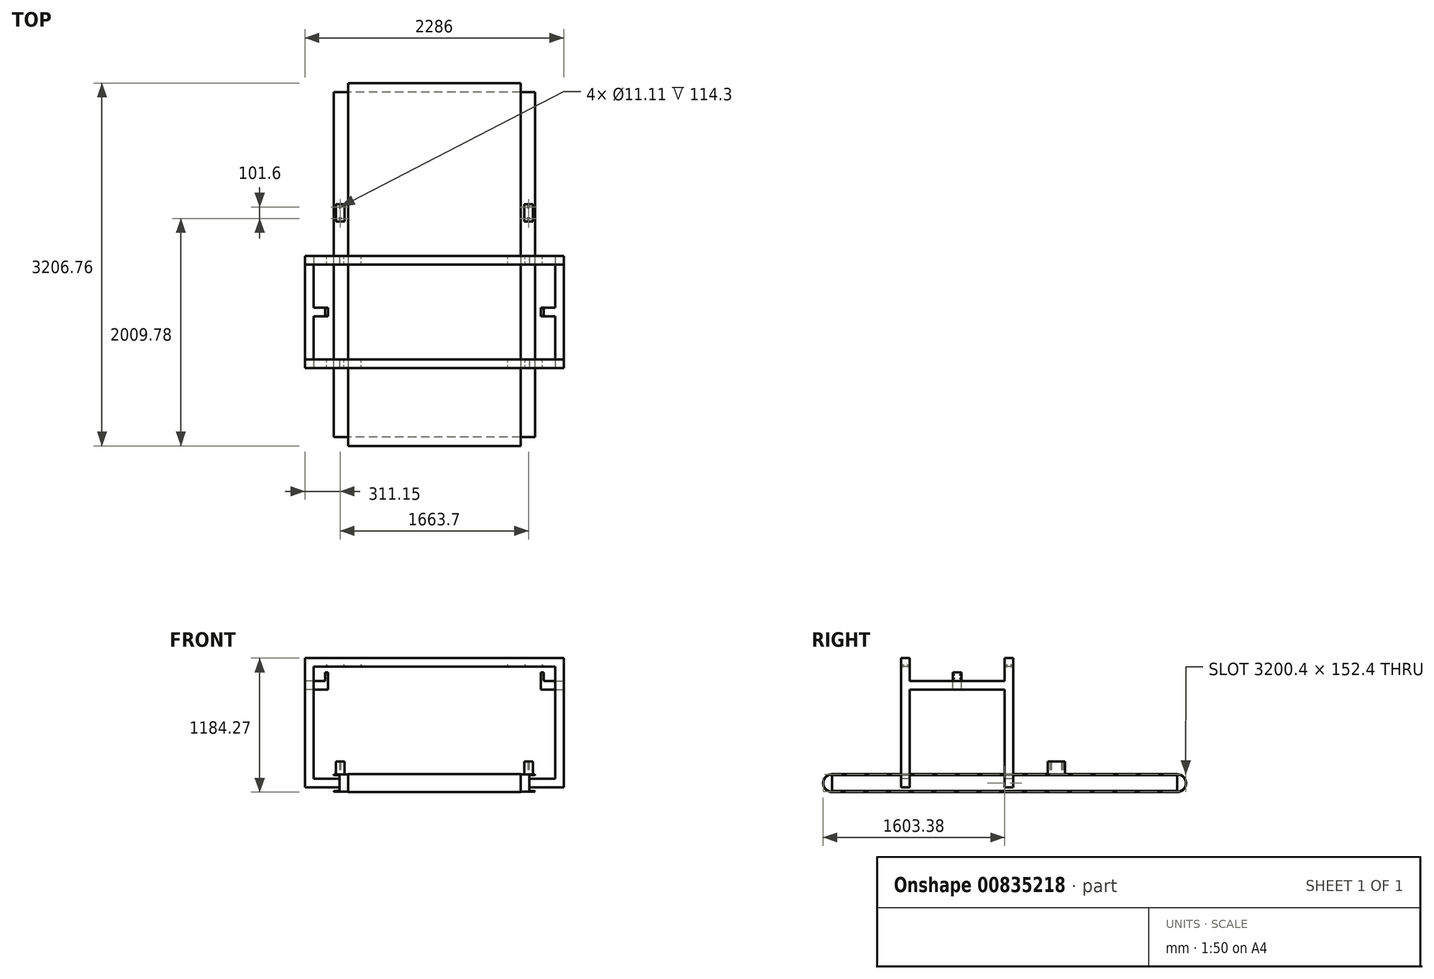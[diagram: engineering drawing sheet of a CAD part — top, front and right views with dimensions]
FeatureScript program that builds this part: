
annotation { "Feature Type Name" : "Feature", "Feature Type Description" : "" }
export const myFeature = defineFeature(function(context is Context, id is Id, definition is map)
    precondition{}
    {
        {
            var Q0;
            Q0=qCreatedBy(makeId("Right.planeOp"),FACE);
            var sketch = newSketch(context, id + "F0", { "sketchPlane" : qUnion([Q0])});
            skLineSegment(sketch, "E0.bottom", {"start": v(1524, 1.59) * mm, "end": v(-1524, 1.59) * mm});
            skLineSegment(sketch, "E0.top", {"start": v(1524, -1.59) * mm, "end": v(-1524, -1.59) * mm});
            skLineSegment(sketch, "E0.left", {"start": v(1524, 1.59) * mm, "end": v(1524, -1.59) * mm});
            skPoint(sketch, "E0.middle", {"position": v(0, 0) * mm});
            skArc(sketch, "E1", {"start": v(-1524, -1.59) * mm, "mid": v(-1600.2, -77.79) * mm, "end": v(-1524, -153.99) * mm});
            skLineSegment(sketch, "E2.0", {"start": v(1524, -153.99) * mm, "end": v(-1524, -153.99) * mm});
            skLineSegment(sketch, "E3.0", {"start": v(1524, -157.16) * mm, "end": v(-1524, -157.16) * mm});
            skArc(sketch, "E4", {"start": v(-1524, 1.59) * mm, "mid": v(-1603.38, -77.79) * mm, "end": v(-1524, -157.16) * mm});
            skArc(sketch, "E5", {"start": v(1524, -153.99) * mm, "mid": v(1600.2, -77.79) * mm, "end": v(1524, -1.59) * mm});
            skArc(sketch, "E6", {"start": v(1524, -157.16) * mm, "mid": v(1603.38, -77.79) * mm, "end": v(1524, 1.59) * mm});
            skSolve(sketch);
        }
        {
            var Q0;
            Q0 = qSketchRegion(id + "F0", true);
            extrude(context, id + "F1", {"entities" : qUnion([Q0]), "endBound" : BoundingType.SYMMETRIC, "depth" : 1524 * mm, "offsetDistance" : 25.4 * mm});
        }
        {
            var Q0;
            Q0=qCreatedBy(makeId("Front.planeOp"),FACE);
            var sketch = newSketch(context, id + "F2", { "sketchPlane" : qUnion([Q0])});
            skLineSegment(sketch, "E7", {"start": v(889, -153.99) * mm, "end": v(-889, -153.99) * mm});
            skLineSegment(sketch, "E8", {"start": v(-889, -153.99) * mm, "end": v(-889, -147.64) * mm});
            skLineSegment(sketch, "E9", {"start": v(-889, -147.64) * mm, "end": v(-838.2, -147.64) * mm});
            skLineSegment(sketch, "E10", {"start": v(-838.2, -147.64) * mm, "end": v(-838.2, -7.94) * mm});
            skLineSegment(sketch, "E11", {"start": v(-838.2, -7.94) * mm, "end": v(-889, -7.94) * mm});
            skLineSegment(sketch, "E12", {"start": v(0, 86.65) * mm, "end": v(0, -258.01) * mm, "construction": true});
            skLineSegment(sketch, "E13.MirrorCS", {"start": v(838.2, -147.64) * mm, "end": v(838.2, -7.94) * mm});
            skLineSegment(sketch, "E14.MirrorCS", {"start": v(838.2, -7.94) * mm, "end": v(889, -7.94) * mm});
            skLineSegment(sketch, "E15.MirrorCS", {"start": v(889, -147.64) * mm, "end": v(838.2, -147.64) * mm});
            skLineSegment(sketch, "E16.MirrorCS", {"start": v(889, -153.99) * mm, "end": v(889, -147.64) * mm});
            skLineSegment(sketch, "E17.MirrorCS", {"start": v(889, -7.94) * mm, "end": v(889, -1.59) * mm});
            skLineSegment(sketch, "E18", {"start": v(-889, -7.94) * mm, "end": v(-889, -1.59) * mm});
            skLineSegment(sketch, "E19", {"start": v(-889, -1.59) * mm, "end": v(889, -1.59) * mm});
            skSolve(sketch);
        }
        {
            var Q0;
            Q0 = qSketchRegion(id + "F2", true);
            extrude(context, id + "F3", {"entities" : qUnion([Q0]), "endBound" : BoundingType.SYMMETRIC, "depth" : 3048 * mm, "offsetDistance" : 25.4 * mm});
        }
        {
            var Q0;
            Q0=makeQuery(id+"F3.opExtrude","SWEPT_EDGE",EDGE,{"disambiguationData":[OSD([sQuery(id+"F2.wireOp",EDGE,"E11"),sQuery(id+"F2.wireOp",EDGE,"E18")])]});
            var Q1;
            Q1=makeQuery(id+"F3.opExtrude","SWEPT_EDGE",EDGE,{"disambiguationData":[OSD([sQuery(id+"F2.wireOp",EDGE,"E10"),sQuery(id+"F2.wireOp",EDGE,"E11")])]});
            var Q2;
            Q2=makeQuery(id+"F3.opExtrude","SWEPT_EDGE",EDGE,{"disambiguationData":[OSD([sQuery(id+"F2.wireOp",EDGE,"E9"),sQuery(id+"F2.wireOp",EDGE,"E10")])]});
            var Q3;
            Q3=makeQuery(id+"F3.opExtrude","SWEPT_EDGE",EDGE,{"disambiguationData":[OSD([sQuery(id+"F2.wireOp",EDGE,"E8"),sQuery(id+"F2.wireOp",EDGE,"E9")])]});
            var Q4;
            Q4=makeQuery(id+"F3.opExtrude","SWEPT_EDGE",EDGE,{"disambiguationData":[OSD([sQuery(id+"F2.wireOp",EDGE,"E14.MirrorCS"),sQuery(id+"F2.wireOp",EDGE,"E17.MirrorCS")])]});
            var Q5;
            Q5=makeQuery(id+"F3.opExtrude","SWEPT_EDGE",EDGE,{"disambiguationData":[OSD([sQuery(id+"F2.wireOp",EDGE,"E13.MirrorCS"),sQuery(id+"F2.wireOp",EDGE,"E15.MirrorCS")])]});
            var Q6;
            Q6=makeQuery(id+"F3.opExtrude","SWEPT_EDGE",EDGE,{"disambiguationData":[OSD([sQuery(id+"F2.wireOp",EDGE,"E15.MirrorCS"),sQuery(id+"F2.wireOp",EDGE,"E16.MirrorCS")])]});
            var Q7;
            Q7=makeQuery(id+"F3.opExtrude","SWEPT_EDGE",EDGE,{"disambiguationData":[OSD([sQuery(id+"F2.wireOp",EDGE,"E13.MirrorCS"),sQuery(id+"F2.wireOp",EDGE,"E14.MirrorCS")])]});
            fillet(context, id + "F4", {"entities" : qUnion([Q0, Q1, Q2, Q3, Q4, Q5, Q6, Q7]), "radius" : 6.35 * mm, "tangentPropagation" : true, "allowEdgeOverflow" : false});
        }
        {
            var Q0;
            Q0=makeQuery(id+"F3.opExtrude","SWEPT_FACE",FACE,{"disambiguationData":[OSD([sQuery(id+"F2.wireOp",EDGE,"E19")])]});
            var sketch = newSketch(context, id + "F5", { "sketchPlane" : qUnion([Q0])});
            skLineSegment(sketch, "E20", {"start": v(793.75, 533.4) * mm, "end": v(793.75, 381) * mm});
            skLineSegment(sketch, "E21", {"start": v(793.75, 533.4) * mm, "end": v(869.95, 533.4) * mm});
            skLineSegment(sketch, "E22", {"start": v(869.95, 533.4) * mm, "end": v(869.95, 381) * mm});
            skLineSegment(sketch, "E23", {"start": v(869.95, 381) * mm, "end": v(793.75, 381) * mm});
            skLineSegment(sketch, "E24.bottom", {"start": v(-793.75, 533.4) * mm, "end": v(-869.95, 533.4) * mm});
            skLineSegment(sketch, "E24.top", {"start": v(-793.75, 381) * mm, "end": v(-869.95, 381) * mm});
            skLineSegment(sketch, "E24.left", {"start": v(-793.75, 533.4) * mm, "end": v(-793.75, 381) * mm});
            skLineSegment(sketch, "E24.right", {"start": v(-869.95, 533.4) * mm, "end": v(-869.95, 381) * mm});
            skCircle(sketch, "E25", {"center": v(-831.85, 508) * mm, "radius": 5.56 * mm});
            skCircle(sketch, "E26", {"center": v(-831.85, 406.4) * mm, "radius": 5.56 * mm});
            skCircle(sketch, "E27", {"center": v(831.85, 508) * mm, "radius": 5.56 * mm});
            skCircle(sketch, "E28", {"center": v(831.85, 406.4) * mm, "radius": 5.56 * mm});
            skSolve(sketch);
        }
        {
            var Q0;
            Q0 = qSketchRegion(id + "F5", true);
            extrude(context, id + "F6", {"entities" : qUnion([Q0]), "operationType" : NewBodyOperationType.ADD, "depth" : 114.3 * mm, "offsetDistance" : 25.4 * mm});
        }
        {
            var Q0;
            Q0=qCreatedBy(makeId("Front.planeOp"),FACE);
            var sketch = newSketch(context, id + "F7", { "sketchPlane" : qUnion([Q0])});
            skLineSegment(sketch, "E29", {"start": v(838.2, -39.69) * mm, "end": v(1066.8, -39.69) * mm});
            skLineSegment(sketch, "E30", {"start": v(1066.8, -39.69) * mm, "end": v(1066.8, 950.91) * mm});
            skLineSegment(sketch, "E31", {"start": v(1066.8, 950.91) * mm, "end": v(-1066.8, 950.91) * mm});
            skLineSegment(sketch, "E32", {"start": v(-1066.8, 950.91) * mm, "end": v(-1066.8, -39.69) * mm});
            skLineSegment(sketch, "E33", {"start": v(-1066.8, -39.69) * mm, "end": v(-838.2, -39.69) * mm});
            skLineSegment(sketch, "E34", {"start": v(-838.2, -39.69) * mm, "end": v(-838.2, -115.89) * mm});
            skLineSegment(sketch, "E35", {"start": v(-838.2, -115.89) * mm, "end": v(-1143, -115.89) * mm});
            skLineSegment(sketch, "E36", {"start": v(-1143, -115.89) * mm, "end": v(-1143, 1027.11) * mm});
            skLineSegment(sketch, "E37", {"start": v(-1143, 1027.11) * mm, "end": v(1143, 1027.11) * mm});
            skLineSegment(sketch, "E38", {"start": v(1143, 1027.11) * mm, "end": v(1143, -115.89) * mm});
            skLineSegment(sketch, "E39", {"start": v(1143, -115.89) * mm, "end": v(838.2, -115.89) * mm});
            skLineSegment(sketch, "E40", {"start": v(838.2, -115.89) * mm, "end": v(838.2, -39.69) * mm});
            skSolve(sketch);
        }
        {
            var Q0;
            Q0 = qSketchRegion(id + "F7", true);
            extrude(context, id + "F8", {"entities" : qUnion([Q0]), "operationType" : NewBodyOperationType.ADD, "oppositeDirection" : true, "depth" : 76.2 * mm, "offsetDistance" : 25.4 * mm});
        }
        {
            var Q0;
            Q0=makeQuery(id+"F8.opExtrude","CAP_FACE",FACE,{"disambiguationData":[OSD([sQuery(id+"F7.wireOp",EDGE,"E29"),sQuery(id+"F7.wireOp",EDGE,"E30"),sQuery(id+"F7.wireOp",EDGE,"E31"),sQuery(id+"F7.wireOp",EDGE,"E32"),sQuery(id+"F7.wireOp",EDGE,"E33"),sQuery(id+"F7.wireOp",EDGE,"E34"),sQuery(id+"F7.wireOp",EDGE,"E35"),sQuery(id+"F7.wireOp",EDGE,"E36"),sQuery(id+"F7.wireOp",EDGE,"E37"),sQuery(id+"F7.wireOp",EDGE,"E38"),sQuery(id+"F7.wireOp",EDGE,"E39"),sQuery(id+"F7.wireOp",EDGE,"E40")])],"isStart":true});
            cPlane(context, id + "F9", {"entities" : qUnion([Q0]), "cplaneType" : CPlaneType.OFFSET, "offset" : 914.4 * mm, "width" : 152.4 * mm, "height" : 152.4 * mm});
        }
        {
            var Q0;
            Q0=qCreatedBy(id+"F9.planeOp",FACE);
            var sketch = newSketch(context, id + "F10", { "sketchPlane" : qUnion([Q0])});
            skLineSegment(sketch, "E41", {"start": v(838.2, -39.69) * mm, "end": v(1066.8, -39.69) * mm});
            skLineSegment(sketch, "E42", {"start": v(1066.8, -39.69) * mm, "end": v(1066.8, 950.91) * mm});
            skLineSegment(sketch, "E43", {"start": v(1066.8, 950.91) * mm, "end": v(-1066.8, 950.91) * mm});
            skLineSegment(sketch, "E44", {"start": v(-1066.8, 950.91) * mm, "end": v(-1066.8, -39.69) * mm});
            skLineSegment(sketch, "E45", {"start": v(-1066.8, -39.69) * mm, "end": v(-838.2, -39.69) * mm});
            skLineSegment(sketch, "E46", {"start": v(-838.2, -39.69) * mm, "end": v(-838.2, -115.89) * mm});
            skLineSegment(sketch, "E47", {"start": v(-838.2, -115.89) * mm, "end": v(-1143, -115.89) * mm});
            skLineSegment(sketch, "E48", {"start": v(-1143, -115.89) * mm, "end": v(-1143, 1027.11) * mm});
            skLineSegment(sketch, "E49", {"start": v(-1143, 1027.11) * mm, "end": v(1143, 1027.11) * mm});
            skLineSegment(sketch, "E50", {"start": v(1143, 1027.11) * mm, "end": v(1143, -115.89) * mm});
            skLineSegment(sketch, "E51", {"start": v(1143, -115.89) * mm, "end": v(838.2, -115.89) * mm});
            skLineSegment(sketch, "E52", {"start": v(838.2, -115.89) * mm, "end": v(838.2, -39.69) * mm});
            skSolve(sketch);
        }
        {
            var Q0;
            Q0 = qSketchRegion(id + "F10", true);
            extrude(context, id + "F11", {"entities" : qUnion([Q0]), "operationType" : NewBodyOperationType.ADD, "oppositeDirection" : true, "depth" : 76.2 * mm, "offsetDistance" : 25.4 * mm});
        }
        {
            var Q0;
            Q0=makeQuery(id+"F8.opExtrude","SWEPT_FACE",FACE,{"disambiguationData":[OSD([sQuery(id+"F7.wireOp",EDGE,"E31")])]});
            var sketch = newSketch(context, id + "F12", { "sketchPlane" : qUnion([Q0])});
            skPoint(sketch, "E53", {"position": v(-952.5, -19.05) * mm});
            skPoint(sketch, "E54", {"position": v(-952.5, -57.15) * mm});
            skPoint(sketch, "E55", {"position": v(-800.1, -57.15) * mm});
            skPoint(sketch, "E56", {"position": v(-800.1, -19.05) * mm});
            skPoint(sketch, "E57", {"position": v(-647.7, -19.05) * mm});
            skPoint(sketch, "E58", {"position": v(-647.7, -57.15) * mm});
            skPoint(sketch, "E59", {"position": v(952.5, -19.05) * mm});
            skPoint(sketch, "E60", {"position": v(800.1, -19.05) * mm});
            skPoint(sketch, "E61", {"position": v(647.7, -19.05) * mm});
            skPoint(sketch, "E62", {"position": v(647.7, -57.15) * mm});
            skPoint(sketch, "E63", {"position": v(800.1, -57.15) * mm});
            skPoint(sketch, "E64", {"position": v(952.5, -57.15) * mm});
            skPoint(sketch, "E65", {"position": v(-952.5, 857.25) * mm});
            skPoint(sketch, "E66", {"position": v(-952.5, 895.35) * mm});
            skPoint(sketch, "E67", {"position": v(-800.1, 895.35) * mm});
            skPoint(sketch, "E68", {"position": v(-800.1, 857.25) * mm});
            skPoint(sketch, "E69", {"position": v(-647.7, 857.25) * mm});
            skPoint(sketch, "E70", {"position": v(-647.7, 895.35) * mm});
            skPoint(sketch, "E71", {"position": v(647.7, 857.25) * mm});
            skPoint(sketch, "E72", {"position": v(647.7, 895.35) * mm});
            skPoint(sketch, "E73", {"position": v(800.1, 857.25) * mm});
            skPoint(sketch, "E74", {"position": v(800.1, 895.35) * mm});
            skPoint(sketch, "E75", {"position": v(952.5, 857.25) * mm});
            skPoint(sketch, "E76", {"position": v(952.5, 895.35) * mm});
            skSolve(sketch);
        }
        {
            var Q0;
            Q0=sQuery(id+"F12.wireOp",VERTEX,"E53");
            var Q1;
            Q1=sQuery(id+"F12.wireOp",VERTEX,"E54");
            var Q2;
            Q2=sQuery(id+"F12.wireOp",VERTEX,"E56");
            var Q3;
            Q3=sQuery(id+"F12.wireOp",VERTEX,"E55");
            var Q4;
            Q4=sQuery(id+"F12.wireOp",VERTEX,"E58");
            var Q5;
            Q5=sQuery(id+"F12.wireOp",VERTEX,"E57");
            var Q6;
            Q6=sQuery(id+"F12.wireOp",VERTEX,"E62");
            var Q7;
            Q7=sQuery(id+"F12.wireOp",VERTEX,"E61");
            var Q8;
            Q8=sQuery(id+"F12.wireOp",VERTEX,"E63");
            var Q9;
            Q9=sQuery(id+"F12.wireOp",VERTEX,"E60");
            var Q10;
            Q10=sQuery(id+"F12.wireOp",VERTEX,"E59");
            var Q11;
            Q11=sQuery(id+"F12.wireOp",VERTEX,"E64");
            var Q12;
            Q12=sQuery(id+"F12.wireOp",VERTEX,"E65");
            var Q13;
            Q13=sQuery(id+"F12.wireOp",VERTEX,"E66");
            var Q14;
            Q14=sQuery(id+"F12.wireOp",VERTEX,"E67");
            var Q15;
            Q15=sQuery(id+"F12.wireOp",VERTEX,"E68");
            var Q16;
            Q16=sQuery(id+"F12.wireOp",VERTEX,"E69");
            var Q17;
            Q17=sQuery(id+"F12.wireOp",VERTEX,"E70");
            var Q18;
            Q18=sQuery(id+"F12.wireOp",VERTEX,"E72");
            var Q19;
            Q19=sQuery(id+"F12.wireOp",VERTEX,"E71");
            var Q20;
            Q20=sQuery(id+"F12.wireOp",VERTEX,"E73");
            var Q21;
            Q21=sQuery(id+"F12.wireOp",VERTEX,"E74");
            var Q22;
            Q22=sQuery(id+"F12.wireOp",VERTEX,"E76");
            var Q23;
            Q23=sQuery(id+"F12.wireOp",VERTEX,"E75");
            var Q24;
            Q24=makeQuery(id+"F3.opExtrude","SWEPT_BODY",BODY,{"disambiguationData":[OSD([sQuery(id+"F2.wireOp",EDGE,"E7"),sQuery(id+"F2.wireOp",EDGE,"E8"),sQuery(id+"F2.wireOp",EDGE,"E9"),sQuery(id+"F2.wireOp",EDGE,"E10"),sQuery(id+"F2.wireOp",EDGE,"E11"),sQuery(id+"F2.wireOp",EDGE,"E13.MirrorCS"),sQuery(id+"F2.wireOp",EDGE,"E14.MirrorCS"),sQuery(id+"F2.wireOp",EDGE,"E15.MirrorCS"),sQuery(id+"F2.wireOp",EDGE,"E16.MirrorCS"),sQuery(id+"F2.wireOp",EDGE,"E17.MirrorCS"),sQuery(id+"F2.wireOp",EDGE,"E18"),sQuery(id+"F2.wireOp",EDGE,"E19")])]});
            hole(context, id + "F13", {"style" : HoleStyle.SIMPLE, "endStyle" : HoleEndStyle.BLIND, "standardTappedOrClearance" : lookupTablePath({ "standard" : "ANSI", "engagement" : "75%", "pitch" : "20 tpi", "size" : "1/4", "type" : "Tapped" }), "standardBlindInLast" : lookupTablePath({ "standard" : "ANSI", "engagement" : "75%", "pitch" : "20 tpi", "size" : "1/4", "type" : "Tapped" }), "holeDiameter" : 5.1 * mm, "majorDiameter" : 6.35 * mm, "showTappedDepth" : true, "holeDepth" : 16.5 * mm, "isTappedThrough" : true, "tappedDepth" : 12.7 * mm, "tapClearance" : 3, "startFromSketch" : true, "locations" : qUnion([Q0, Q1, Q2, Q3, Q4, Q5, Q6, Q7, Q8, Q9, Q10, Q11, Q12, Q13, Q14, Q15, Q16, Q17, Q18, Q19, Q20, Q21, Q22, Q23]), "scope" : qUnion([Q24])});
        }
        {
            var Q0;
            Q0=makeQuery(id+"F8.opExtrude","CAP_FACE",FACE,{"disambiguationData":[OSD([sQuery(id+"F7.wireOp",EDGE,"E29"),sQuery(id+"F7.wireOp",EDGE,"E30"),sQuery(id+"F7.wireOp",EDGE,"E31"),sQuery(id+"F7.wireOp",EDGE,"E32"),sQuery(id+"F7.wireOp",EDGE,"E33"),sQuery(id+"F7.wireOp",EDGE,"E34"),sQuery(id+"F7.wireOp",EDGE,"E35"),sQuery(id+"F7.wireOp",EDGE,"E36"),sQuery(id+"F7.wireOp",EDGE,"E37"),sQuery(id+"F7.wireOp",EDGE,"E38"),sQuery(id+"F7.wireOp",EDGE,"E39"),sQuery(id+"F7.wireOp",EDGE,"E40")])],"isStart":true});
            var sketch = newSketch(context, id + "F14", { "sketchPlane" : qUnion([Q0])});
            skLineSegment(sketch, "E77.bottom", {"start": v(1066.8, 825.51) * mm, "end": v(1143, 825.51) * mm});
            skLineSegment(sketch, "E77.top", {"start": v(1066.8, 749.31) * mm, "end": v(1143, 749.31) * mm});
            skLineSegment(sketch, "E77.left", {"start": v(1066.8, 825.51) * mm, "end": v(1066.8, 749.31) * mm});
            skLineSegment(sketch, "E77.right", {"start": v(1143, 825.51) * mm, "end": v(1143, 749.31) * mm});
            skSolve(sketch);
        }
        {
            var Q0;
            Q0 = qSketchRegion(id + "F14", true);
            extrude(context, id + "F15", {"entities" : qUnion([Q0]), "operationType" : NewBodyOperationType.ADD, "endBound" : BoundingType.UP_TO_NEXT, "depth" : 25.4 * mm, "offsetDistance" : 25.4 * mm});
        }
        {
            var Q0;
            Q0=makeQuery(id+"F15.opExtrude","SWEPT_FACE",FACE,{"disambiguationData":[OSD([sQuery(id+"F14.wireOp",EDGE,"E77.bottom")])]});
            var sketch = newSketch(context, id + "F16", { "sketchPlane" : qUnion([Q0])});
            skLineSegment(sketch, "E78.bottom", {"start": v(1066.8, -381) * mm, "end": v(939.8, -381) * mm});
            skLineSegment(sketch, "E78.top", {"start": v(1066.8, -457.2) * mm, "end": v(939.8, -457.2) * mm});
            skLineSegment(sketch, "E78.left", {"start": v(1066.8, -381) * mm, "end": v(1066.8, -457.2) * mm});
            skLineSegment(sketch, "E78.right", {"start": v(939.8, -381) * mm, "end": v(939.8, -457.2) * mm});
            skPoint(sketch, "E78.middle", {"position": v(1003.3, -419.1) * mm});
            skSolve(sketch);
        }
        {
            var Q0;
            Q0 = qSketchRegion(id + "F16", true);
            var Q1;
            Q1=makeQuery(id+"F15.opExtrude","SWEPT_FACE",FACE,{"disambiguationData":[OSD([sQuery(id+"F14.wireOp",EDGE,"E77.top")])]});
            extrude(context, id + "F17", {"entities" : qUnion([Q0]), "operationType" : NewBodyOperationType.ADD, "endBound" : BoundingType.UP_TO_SURFACE, "oppositeDirection" : true, "depth" : 25.4 * mm, "endBoundEntityFace" : qUnion([Q1]), "offsetDistance" : 25.4 * mm});
        }
        {
            var Q0;
            Q0=makeQuery(id+"F15.opExtrude","SWEPT_FACE",FACE,{"disambiguationData":[OSD([sQuery(id+"F14.wireOp",EDGE,"E77.bottom")])]});
            var sketch = newSketch(context, id + "F18", { "sketchPlane" : qUnion([Q0])});
            skLineSegment(sketch, "E79.bottom", {"start": v(939.8, -381) * mm, "end": v(965.2, -381) * mm});
            skLineSegment(sketch, "E79.top", {"start": v(939.8, -457.2) * mm, "end": v(965.2, -457.2) * mm});
            skLineSegment(sketch, "E79.left", {"start": v(939.8, -381) * mm, "end": v(939.8, -457.2) * mm});
            skLineSegment(sketch, "E79.right", {"start": v(965.2, -381) * mm, "end": v(965.2, -457.2) * mm});
            skPoint(sketch, "E79.middle", {"position": v(952.5, -419.1) * mm});
            skSolve(sketch);
        }
        {
            var Q0;
            Q0 = qSketchRegion(id + "F18", true);
            extrude(context, id + "F19", {"entities" : qUnion([Q0]), "operationType" : NewBodyOperationType.ADD, "depth" : 76.2 * mm, "offsetDistance" : 25.4 * mm});
        }
        {
            var Q0;
            Q0=makeQuery(id+"F19.opExtrude","SWEPT_FACE",FACE,{"disambiguationData":[OSD([sQuery(id+"F18.wireOp",EDGE,"E79.right")])]});
            var sketch = newSketch(context, id + "F20", { "sketchPlane" : qUnion([Q0])});
            skLineSegment(sketch, "E80.bottom", {"start": v(-389.73, 879.88) * mm, "end": v(-448.47, 879.88) * mm, "construction": true});
            skLineSegment(sketch, "E80.top", {"start": v(-389.73, 847.34) * mm, "end": v(-448.47, 847.34) * mm, "construction": true});
            skLineSegment(sketch, "E80.left", {"start": v(-389.73, 879.88) * mm, "end": v(-389.73, 847.34) * mm, "construction": true});
            skLineSegment(sketch, "E80.right", {"start": v(-448.47, 879.88) * mm, "end": v(-448.47, 847.34) * mm, "construction": true});
            skPoint(sketch, "E80.middle", {"position": v(-419.1, 863.61) * mm});
            skPoint(sketch, "E81", {"position": v(-448.47, 879.88) * mm});
            skPoint(sketch, "E82", {"position": v(-448.47, 847.34) * mm});
            skPoint(sketch, "E83", {"position": v(-389.73, 847.34) * mm});
            skPoint(sketch, "E84", {"position": v(-389.73, 879.88) * mm});
            skSolve(sketch);
        }
        {
            var Q0;
            Q0=sQuery(id+"F20.wireOp",VERTEX,"E81");
            var Q1;
            Q1=sQuery(id+"F20.wireOp",VERTEX,"E82");
            var Q2;
            Q2=sQuery(id+"F20.wireOp",VERTEX,"E83");
            var Q3;
            Q3=sQuery(id+"F20.wireOp",VERTEX,"E84");
            var Q4;
            Q4=makeQuery(id+"F3.opExtrude","SWEPT_BODY",BODY,{"disambiguationData":[OSD([sQuery(id+"F2.wireOp",EDGE,"E7"),sQuery(id+"F2.wireOp",EDGE,"E8"),sQuery(id+"F2.wireOp",EDGE,"E9"),sQuery(id+"F2.wireOp",EDGE,"E10"),sQuery(id+"F2.wireOp",EDGE,"E11"),sQuery(id+"F2.wireOp",EDGE,"E13.MirrorCS"),sQuery(id+"F2.wireOp",EDGE,"E14.MirrorCS"),sQuery(id+"F2.wireOp",EDGE,"E15.MirrorCS"),sQuery(id+"F2.wireOp",EDGE,"E16.MirrorCS"),sQuery(id+"F2.wireOp",EDGE,"E17.MirrorCS"),sQuery(id+"F2.wireOp",EDGE,"E18"),sQuery(id+"F2.wireOp",EDGE,"E19")])]});
            hole(context, id + "F21", {"style" : HoleStyle.SIMPLE, "endStyle" : HoleEndStyle.BLIND, "standardTappedOrClearance" : lookupTablePath({ "standard" : "ANSI", "engagement" : "75%", "pitch" : "20 tpi", "size" : "1/4", "type" : "Tapped" }), "standardBlindInLast" : lookupTablePath({ "standard" : "ANSI", "engagement" : "75%", "pitch" : "20 tpi", "size" : "1/4", "type" : "Tapped" }), "holeDiameter" : 5.1 * mm, "majorDiameter" : 6.35 * mm, "showTappedDepth" : true, "holeDepth" : 16.5 * mm, "isTappedThrough" : true, "tappedDepth" : 12.7 * mm, "tapClearance" : 3, "startFromSketch" : true, "locations" : qUnion([Q0, Q1, Q2, Q3]), "scope" : qUnion([Q4])});
        }
        {
            var Q0;
            Q0=makeQuery(id+"F3.opExtrude","SWEPT_BODY",BODY,{"disambiguationData":[OSD([sQuery(id+"F2.wireOp",EDGE,"E7"),sQuery(id+"F2.wireOp",EDGE,"E8"),sQuery(id+"F2.wireOp",EDGE,"E9"),sQuery(id+"F2.wireOp",EDGE,"E10"),sQuery(id+"F2.wireOp",EDGE,"E11"),sQuery(id+"F2.wireOp",EDGE,"E13.MirrorCS"),sQuery(id+"F2.wireOp",EDGE,"E14.MirrorCS"),sQuery(id+"F2.wireOp",EDGE,"E15.MirrorCS"),sQuery(id+"F2.wireOp",EDGE,"E16.MirrorCS"),sQuery(id+"F2.wireOp",EDGE,"E17.MirrorCS"),sQuery(id+"F2.wireOp",EDGE,"E18"),sQuery(id+"F2.wireOp",EDGE,"E19")])]});
            var Q1;
            Q1=qCreatedBy(makeId("Right.planeOp"),FACE);
            mirror(context, id + "F22", {"operationType" : NewBodyOperationType.ADD, "entities" : qUnion([Q0]), "mirrorPlane" : qUnion([Q1])});
        }
    });
